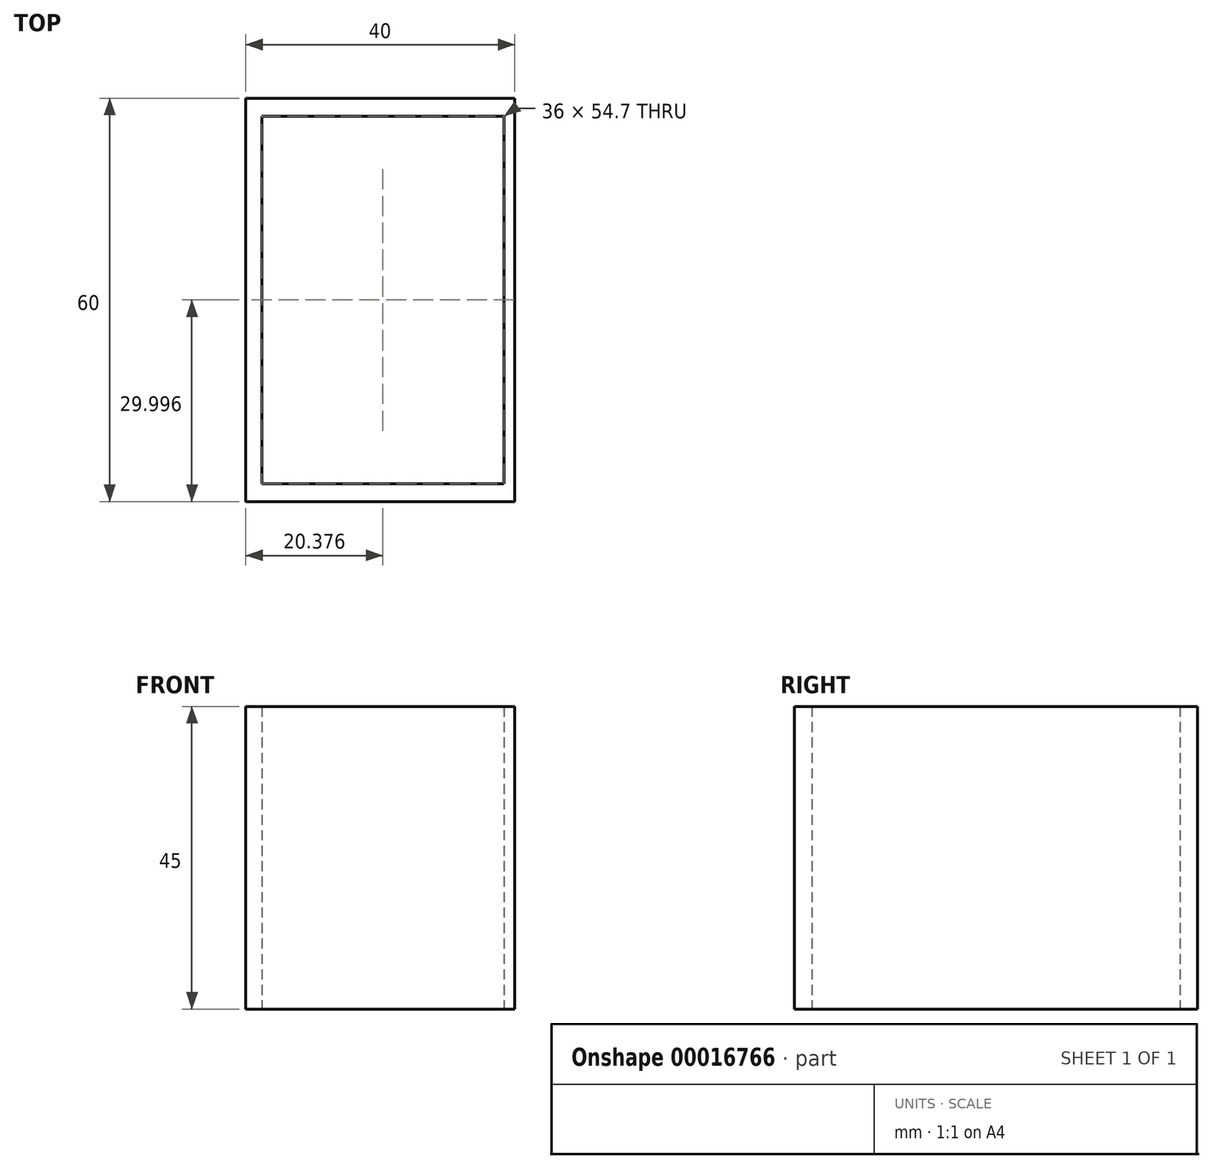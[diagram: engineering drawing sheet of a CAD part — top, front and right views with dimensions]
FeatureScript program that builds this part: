
annotation { "Feature Type Name" : "Feature", "Feature Type Description" : "" }
export const myFeature = defineFeature(function(context is Context, id is Id, definition is map)
    precondition{}
    {
        {
            var Q0;
            Q0=qCreatedBy(makeId("Top.planeOp"),FACE);
            var sketch = newSketch(context, id + "F0", { "sketchPlane" : qUnion([Q0])});
            skLineSegment(sketch, "E0.bottom", {"start": v(-54.7, 64.5) * mm, "end": v(-14.7, 64.5) * mm});
            skLineSegment(sketch, "E0.top", {"start": v(-54.7, 4.5) * mm, "end": v(-14.7, 4.5) * mm});
            skLineSegment(sketch, "E0.left", {"start": v(-54.7, 64.5) * mm, "end": v(-54.7, 4.5) * mm});
            skLineSegment(sketch, "E0.right", {"start": v(-14.7, 64.5) * mm, "end": v(-14.7, 4.5) * mm});
            skLineSegment(sketch, "E1.bottom", {"start": v(-52.32, 61.84) * mm, "end": v(-16.32, 61.84) * mm});
            skLineSegment(sketch, "E1.top", {"start": v(-52.32, 7.14) * mm, "end": v(-16.32, 7.14) * mm});
            skLineSegment(sketch, "E1.left", {"start": v(-52.32, 61.84) * mm, "end": v(-52.32, 7.14) * mm});
            skLineSegment(sketch, "E1.right", {"start": v(-16.32, 61.84) * mm, "end": v(-16.32, 7.14) * mm});
            skSolve(sketch);
        }
        {
            var Q0;
            Q0=makeQuery(id+"F0.imprint","IMPRINT",FACE,{"disambiguationData":[TD([[makeQuery(id+"F0.imprint","IMPRINT",EDGE,{"derivedFrom":sQuery(id+"F0.wireOp",EDGE,"E0.bottom")}),-1.0]])]});
            extrude(context, id + "F1", {"entities" : qUnion([Q0]), "depth" : 20 * mm});
        }
        {
            var Q0;
            Q0=makeQuery(id+"F1.opExtrude","CAP_FACE",FACE,{"disambiguationData":[OSD([sQuery(id+"F0.wireOp",EDGE,"E0.bottom"),sQuery(id+"F0.wireOp",EDGE,"E0.top"),sQuery(id+"F0.wireOp",EDGE,"E0.left"),sQuery(id+"F0.wireOp",EDGE,"E0.right"),sQuery(id+"F0.wireOp",EDGE,"E1.bottom"),sQuery(id+"F0.wireOp",EDGE,"E1.top"),sQuery(id+"F0.wireOp",EDGE,"E1.left"),sQuery(id+"F0.wireOp",EDGE,"E1.right")])],"isStart":false});
            var Q1;
            Q1 = qSketchRegion(id + "F0", true);
            extrude(context, id + "F2", {"entities" : qUnion([Q0, Q1]), "operationType" : NewBodyOperationType.ADD, "depth" : 25 * mm});
        }
    });
